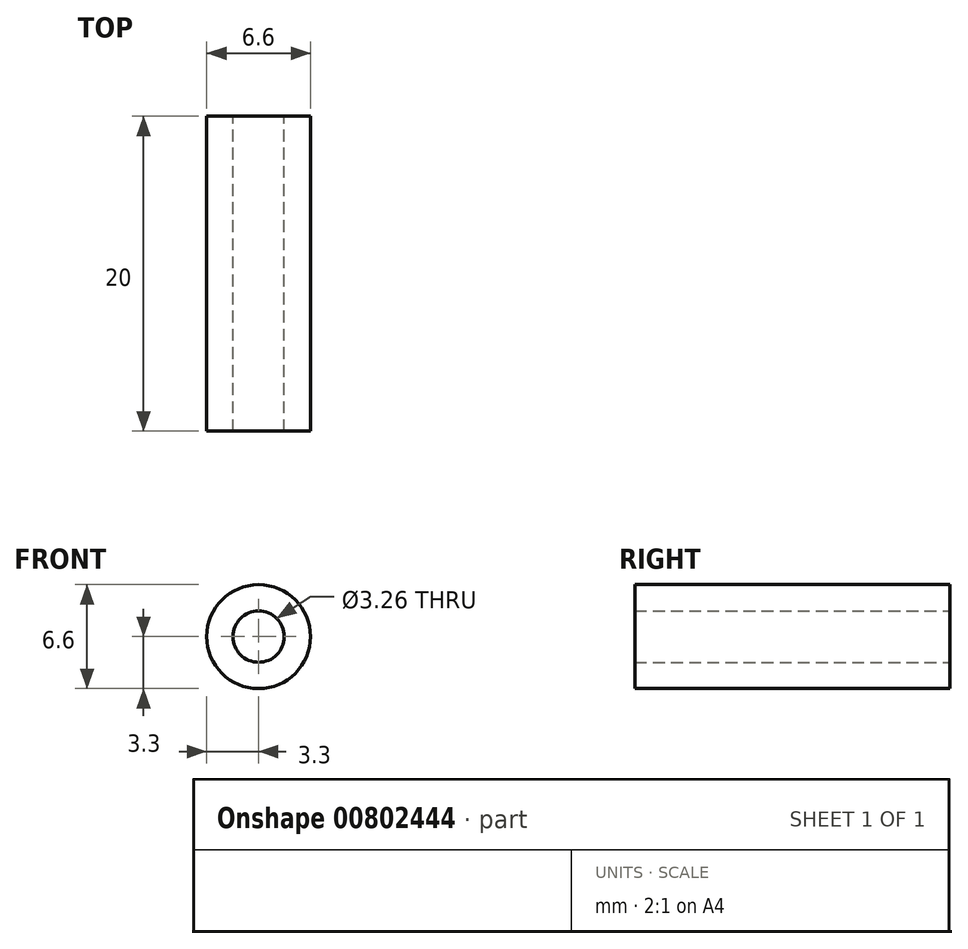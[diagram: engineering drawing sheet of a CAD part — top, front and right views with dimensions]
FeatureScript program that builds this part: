
annotation { "Feature Type Name" : "Feature", "Feature Type Description" : "" }
export const myFeature = defineFeature(function(context is Context, id is Id, definition is map)
    precondition{}
    {
        {
            var Q0;
            Q0=qCreatedBy(makeId("Front.planeOp"),FACE);
            var sketch = newSketch(context, id + "F0", { "sketchPlane" : qUnion([Q0])});
            skCircle(sketch, "E0", {"center": v(0, 0) * mm, "radius": 1.63 * mm});
            skCircle(sketch, "E1", {"center": v(0, 0) * mm, "radius": 3.3 * mm});
            skSolve(sketch);
        }
        {
            var Q0;
            Q0 = qSketchRegion(id + "F0", true);
            extrude(context, id + "F1", {"entities" : qUnion([Q0]), "depth" : 20 * mm, "offsetDistance" : 25 * mm});
        }
    });
